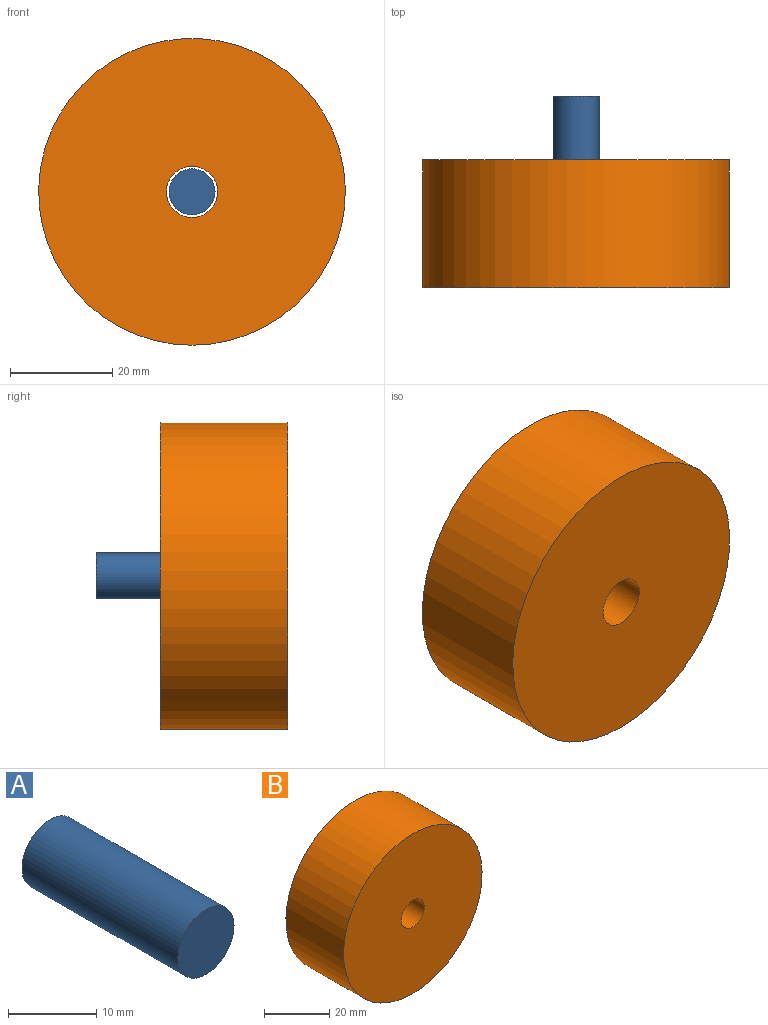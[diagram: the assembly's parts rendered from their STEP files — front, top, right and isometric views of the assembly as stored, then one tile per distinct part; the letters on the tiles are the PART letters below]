
ASSEMBLY  parts=2 mates=1
PART A: 3 faces, bbox 9x25x9 mm
  f0: cylinder r=4.5mm len=25mm, axis (0,-1,0), area 706.9mm2, adj f1,f2
  f1: plane 9x9mm, normal (0,1,0), area 63.6mm2, adj f0
  f2: plane 9x9mm, normal (0,-1,0), area 63.6mm2, adj f0
PART B: 4 faces, bbox 60x25x60 mm
  f0: cylinder r=5mm len=25mm, axis (0,1,0), area 785.4mm2, adj f2,f3
  f1: cylinder r=30mm len=60mm, axis (0,1,0), area 4712.4mm2, adj f2,f3
  f2: plane 60x60mm, normal (0,-1,0), area 2748.9mm2, adj f0,f1
  f3: plane 60x60mm, normal (0,1,0), area 2748.9mm2, adj f0,f1
PLACE A t=(-31.55,46.16,-21.59)mm
PLACE B t=(-6.03,8.66,-0.53)mm
MATE revolute A.f0 <-> B.f0  axis (0,-1,0) through (-6.03,-3.84,-0.53)mm
